# Revit family: Sink-Undermount-Waterworks-Rectangular-Clara
name_source: partatom
category: Plumbing Fixtures
revit_build: Autodesk Revit MEP 2014 (Build: 20140709_2115(x64)
units: mm (PartAtom-declared; Revit-internal decimal feet)

## types (2) — shared parameters
Assembly Code = D2010400
CW Connection = No
Default Elevation = 2' - 10"
Depth = 1' - 2 1/8"
Drain Diameter = 0' - 1 3/8"
Finish = Vitreous China - Waterworks -  White
HW Connection = No
Height = 0' - 8"
Keynote = 22 40 00.A5
Length = 1' - 8 1/16"
Manufacturer = Waterworks
Product Documentation Link = http://assets.waterworks.com
Product Page URL = http://www.waterworks.com
Sanitary Connector = Sanitary Drain
URL = http://www.waterworks.com
Vent Connection = No
Version = 2014 - v1.0a
Warranty = http://www.waterworks.com
Waste Connection = Yes
‌Installation Requirements or Notes = Dimensions of sinks are nominal and are subject to slight variations
zero-valued in all types: CWFU, HWFU, WFU

## per-type parameters (varying)
| type | ADA Compliant | Constraint | Description | Model | Model SKU | Product Name |
| Double Glazed | Yes | 2 | Clara Undermount Rectangular Vitreous China Lavatory Sink Double Glazed | CYLV22 | 11-15689-67913 | Clara Undermount Rectangular Vitreous China Lavatory Sink Double Glazed |
| Single Glazed | No | 1 | Clara Undermount Rectangular Vitreous China Lavatory Sink Single Glazed | CYLV20 | 11-48480-15126 | Clara Undermount Rectangular Vitreous China Lavatory Sink Single Glazed |

## geometry (parser evidence)
native form markers: Sweep x1
no freeform markers — native parametric forms only
